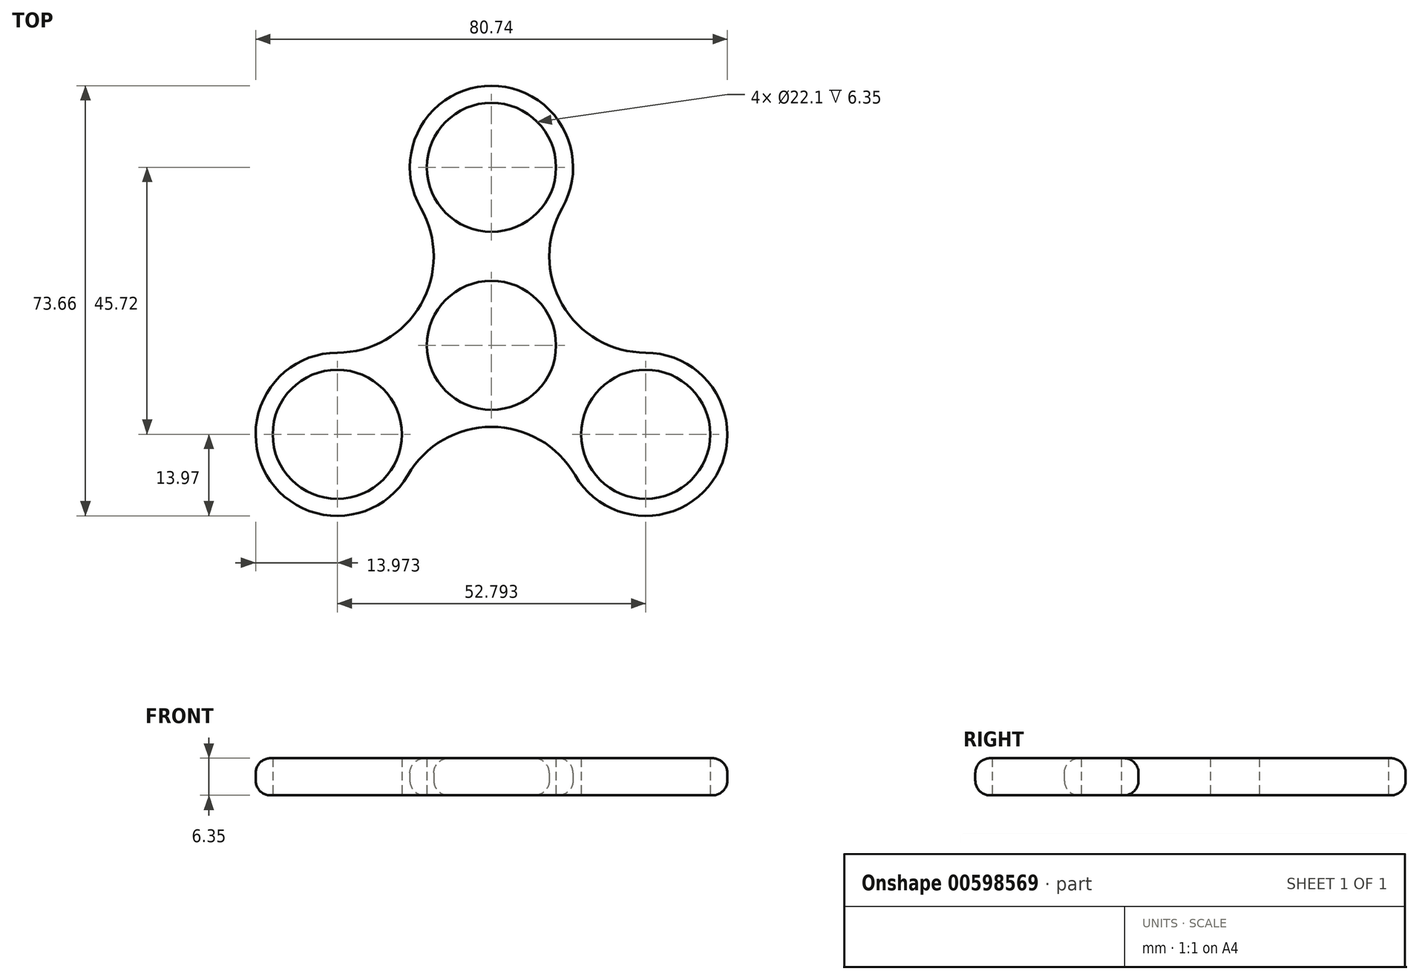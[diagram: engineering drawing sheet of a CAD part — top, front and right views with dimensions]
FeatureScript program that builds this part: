
annotation { "Feature Type Name" : "Feature", "Feature Type Description" : "" }
export const myFeature = defineFeature(function(context is Context, id is Id, definition is map)
    precondition{}
    {
        {
            var Q0;
            Q0=qCreatedBy(makeId("Top.planeOp"),FACE);
            var sketch = newSketch(context, id + "F0", { "sketchPlane" : qUnion([Q0])});
            skCircle(sketch, "E0", {"center": v(0, 0) * mm, "radius": 11.05 * mm});
            skCircle(sketch, "E1", {"center": v(0, 0) * mm, "radius": 13.97 * mm});
            skCircle(sketch, "E2", {"center": v(0, 30.48) * mm, "radius": 11.05 * mm});
            skArc(sketch, "E3", {"start": v(12.1, 23.5) * mm, "mid": v(0, 44.45) * mm, "end": v(-12.1, 23.5) * mm});
            skArc(sketch, "E4.1.0", {"start": v(-26.4, -1.27) * mm, "mid": v(-38.5, -22.22) * mm, "end": v(-14.3, -22.22) * mm});
            skArc(sketch, "E4.2.0", {"start": v(14.3, -22.22) * mm, "mid": v(38.5, -22.23) * mm, "end": v(26.4, -1.27) * mm});
            skCircle(sketch, "E5.1.0", {"center": v(-26.4, -15.24) * mm, "radius": 11.05 * mm});
            skCircle(sketch, "E5.2.0", {"center": v(26.4, -15.24) * mm, "radius": 11.05 * mm});
            skCircle(sketch, "E6", {"center": v(0, 0) * mm, "radius": 44.45 * mm});
            skLineSegment(sketch, "E7", {"start": v(-9.57, 5.52) * mm, "end": v(-12.1, 6.99) * mm});
            skArc(sketch, "E8", {"start": v(-26.4, -1.27) * mm, "mid": v(-12.1, 6.99) * mm, "end": v(-12.1, 23.5) * mm});
            skArc(sketch, "E9.1.0", {"start": v(14.3, -22.22) * mm, "mid": v(0, -13.97) * mm, "end": v(-14.3, -22.22) * mm});
            skArc(sketch, "E9.2.0", {"start": v(12.1, 23.5) * mm, "mid": v(12.1, 6.98) * mm, "end": v(26.4, -1.27) * mm});
            skSolve(sketch);
        }
        {
            var Q0;
            Q0=makeQuery(id+"F0.imprint","IMPRINT",FACE,{"disambiguationData":[TD([[makeQuery(id+"F0.imprint","IMPRINT",EDGE,{"derivedFrom":sQuery(id+"F0.wireOp",EDGE,"E2")}),-1.0]])]});
            var Q1;
            Q1=makeQuery(id+"F0.imprint","IMPRINT",FACE,{"disambiguationData":[TD([[makeQuery(id+"F0.imprint","IMPRINT",EDGE,{"derivedFrom":sQuery(id+"F0.wireOp",EDGE,"E5.1.0")}),-1.0]])]});
            var Q2;
            Q2=makeQuery(id+"F0.imprint","IMPRINT",FACE,{"disambiguationData":[TD([[makeQuery(id+"F0.imprint","IMPRINT",EDGE,{"derivedFrom":sQuery(id+"F0.wireOp",EDGE,"E5.2.0")}),-1.0]])]});
            var Q3;
            Q3=makeQuery(id+"F0.imprint","IMPRINT",FACE,{"disambiguationData":[TD([[makeQuery(id+"F0.imprint","IMPRINT",EDGE,{"derivedFrom":sQuery(id+"F0.wireOp",EDGE,"E0")}),-1.0]])]});
            extrude(context, id + "F1", {"entities" : qUnion([Q0, Q1, Q2, Q3]), "depth" : 6.35 * mm, "offsetDistance" : 25.4 * mm});
        }
        {
            var Q0;
            Q0=makeQuery(id+"F1.opExtrude","CAP_EDGE",EDGE,{"disambiguationData":[OSD([sQuery(id+"F0.wireOp",EDGE,"E4.1.0")])],"isStart":false});
            var Q1;
            Q1=makeQuery(id+"F1.opExtrude","CAP_EDGE",EDGE,{"disambiguationData":[OSD([sQuery(id+"F0.wireOp",EDGE,"E4.1.0")])],"isStart":true});
            fillet(context, id + "F2", {"entities" : qUnion([Q0, Q1]), "radius" : 2.54 * mm, "tangentPropagation" : true, "allowEdgeOverflow" : false});
        }
    });
